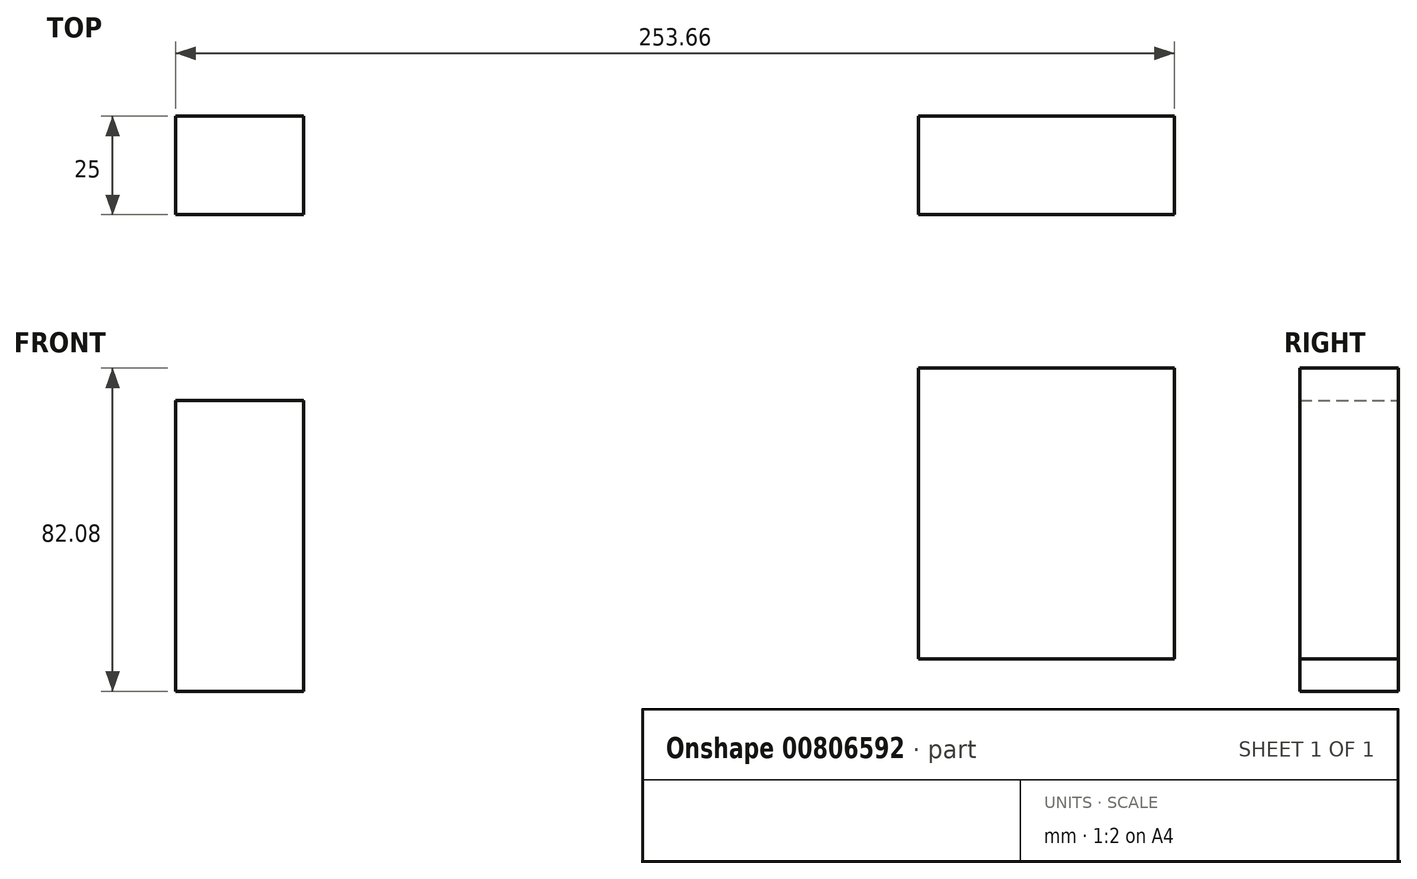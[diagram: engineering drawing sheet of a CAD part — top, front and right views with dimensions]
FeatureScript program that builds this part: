
annotation { "Feature Type Name" : "Feature", "Feature Type Description" : "" }
export const myFeature = defineFeature(function(context is Context, id is Id, definition is map)
    precondition{}
    {
        {
            var Q0;
            Q0=qCreatedBy(makeId("Front.planeOp"),FACE);
            var sketch = newSketch(context, id + "F0", { "sketchPlane" : qUnion([Q0])});
            skLineSegment(sketch, "E0.bottom", {"start": v(-82.83, 36.97) * mm, "end": v(-50.33, 36.97) * mm});
            skLineSegment(sketch, "E0.top", {"start": v(-82.83, -36.91) * mm, "end": v(-50.33, -36.91) * mm});
            skLineSegment(sketch, "E0.left", {"start": v(-82.83, 36.97) * mm, "end": v(-82.83, -36.91) * mm});
            skLineSegment(sketch, "E0.right", {"start": v(-50.33, 36.97) * mm, "end": v(-50.33, -36.91) * mm});
            skSolve(sketch);
        }
        {
            var Q0;
            Q0 = qSketchRegion(id + "F0", true);
            extrude(context, id + "F1", {"entities" : qUnion([Q0]), "depth" : 25 * mm, "offsetDistance" : 25 * mm});
        }
        {
            var Q0;
            Q0=makeQuery(id+"F1.opExtrude","SWEPT_BODY",BODY,{"disambiguationData":[OSD([sQuery(id+"F0.wireOp",EDGE,"E0.bottom"),sQuery(id+"F0.wireOp",EDGE,"E0.top"),sQuery(id+"F0.wireOp",EDGE,"E0.left"),sQuery(id+"F0.wireOp",EDGE,"E0.right")])]});
            var Q1;
            Q1=qCreatedBy(makeId("Right.planeOp"),FACE);
            mirror(context, id + "F2", {"entities" : qUnion([Q0]), "mirrorPlane" : qUnion([Q1])});
        }
        {
            var Q0;
            Q0=makeQuery(id+"F1.opExtrude","SWEPT_BODY",BODY,{"disambiguationData":[OSD([sQuery(id+"F0.wireOp",EDGE,"E0.bottom"),sQuery(id+"F0.wireOp",EDGE,"E0.top"),sQuery(id+"F0.wireOp",EDGE,"E0.left"),sQuery(id+"F0.wireOp",EDGE,"E0.right")])]});
            transform(context, id + "F3", {"entities" : qUnion([Q0]), "transformType" : TransformType.TRANSLATION_3D, "dx" : -88 * mm, "dy" : 0 * mm, "dz" : -8.2 * mm, "makeCopy" : false});
        }
        {
            var Q0;
            Q0=makeQuery(id+"F2.opPattern","COPY",FACE,{"derivedFrom":makeQuery(id+"F1.opExtrude","SWEPT_FACE",FACE,{"disambiguationData":[OSD([sQuery(id+"F0.wireOp",EDGE,"E0.right")])]}),"instanceName":"1"});
            var Q1;
            Q1=makeQuery(id+"F1.opExtrude","CAP_EDGE",EDGE,{"disambiguationData":[OSD([sQuery(id+"F0.wireOp",EDGE,"E0.top")])],"isStart":false});
            sweep(context, id + "F4", {"operationType" : NewBodyOperationType.ADD, "profiles" : qUnion([Q0]), "path" : qUnion([Q1]), "keepProfileOrientation" : true});
        }
    });
